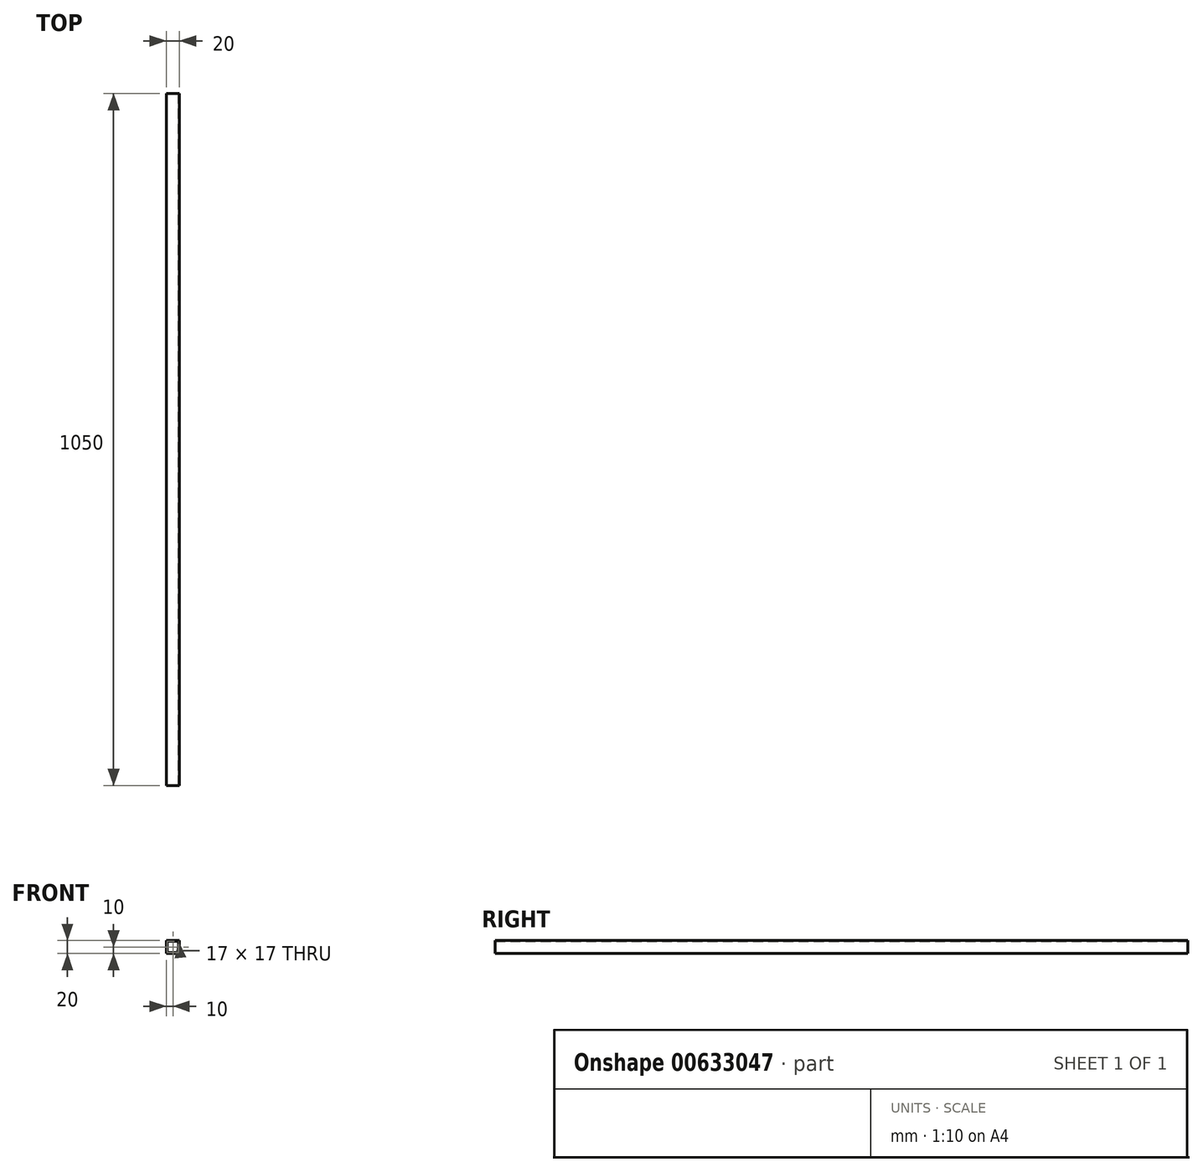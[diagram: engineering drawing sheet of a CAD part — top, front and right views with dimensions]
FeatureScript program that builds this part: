
annotation { "Feature Type Name" : "Feature", "Feature Type Description" : "" }
export const myFeature = defineFeature(function(context is Context, id is Id, definition is map)
    precondition{}
    {
        {
            var Q0;
            Q0=qCreatedBy(makeId("Front.planeOp"),FACE);
            var sketch = newSketch(context, id + "F0", { "sketchPlane" : qUnion([Q0])});
            skLineSegment(sketch, "E0.bottom", {"start": v(0, 0) * mm, "end": v(20, 0) * mm});
            skLineSegment(sketch, "E0.top", {"start": v(0, -20) * mm, "end": v(20, -20) * mm});
            skLineSegment(sketch, "E0.left", {"start": v(0, 0) * mm, "end": v(0, -20) * mm});
            skLineSegment(sketch, "E0.right", {"start": v(20, 0) * mm, "end": v(20, -20) * mm});
            skLineSegment(sketch, "E1.0", {"start": v(1.5, -1.5) * mm, "end": v(18.5, -1.5) * mm});
            skLineSegment(sketch, "E1.1", {"start": v(1.5, -1.5) * mm, "end": v(1.5, -18.5) * mm});
            skLineSegment(sketch, "E1.2", {"start": v(1.5, -18.5) * mm, "end": v(18.5, -18.5) * mm});
            skLineSegment(sketch, "E1.3", {"start": v(18.5, -1.5) * mm, "end": v(18.5, -18.5) * mm});
            skSolve(sketch);
        }
        {
            var Q0;
            Q0=makeQuery(id+"F0.imprint","IMPRINT",FACE,{"disambiguationData":[TD([[makeQuery(id+"F0.imprint","IMPRINT",EDGE,{"derivedFrom":sQuery(id+"F0.wireOp",EDGE,"E0.bottom")}),-1.0]])]});
            extrude(context, id + "F1", {"entities" : qUnion([Q0]), "depth" : 1050 * mm, "offsetDistance" : 25 * mm});
        }
    });
